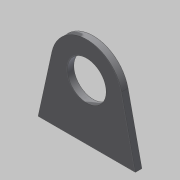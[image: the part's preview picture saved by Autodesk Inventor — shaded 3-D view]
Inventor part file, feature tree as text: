
AUTODESK INVENTOR PART (.ipt)
format: ipt  version: 2020 (Build 240168000, 168)  size: 84,992 bytes
history: native  units: mm
features: other x1, extrude x1
ambient origin geometry x8: Origin, YZ Plane, XZ Plane, XY Plane, X Axis, Y Axis, Z Axis, Center Point
bodies: Body1 (feature_tree)
feature tree (2):
  other  "實體1"
  extrude  "擠出1"  Depth=12.0mm
